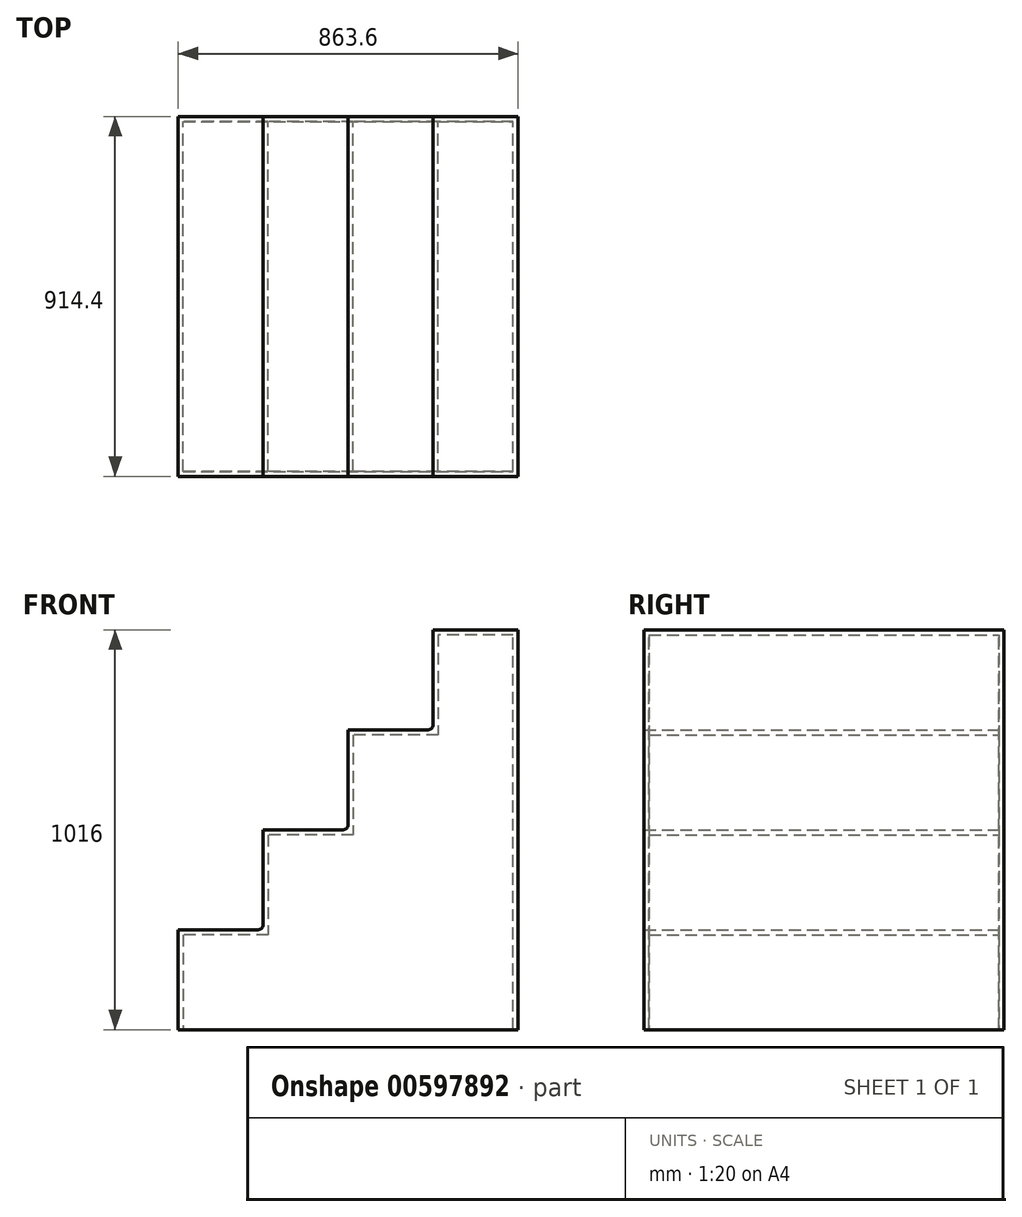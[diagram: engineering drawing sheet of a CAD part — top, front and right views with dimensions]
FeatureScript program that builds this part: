
annotation { "Feature Type Name" : "Feature", "Feature Type Description" : "" }
export const myFeature = defineFeature(function(context is Context, id is Id, definition is map)
    precondition{}
    {
        {
            var Q0;
            Q0=qCreatedBy(makeId("Front.planeOp"),FACE);
            var sketch = newSketch(context, id + "F0", { "sketchPlane" : qUnion([Q0])});
            skLineSegment(sketch, "E0", {"start": v(0, 0) * mm, "end": v(0, 1016) * mm});
            skLineSegment(sketch, "E1", {"start": v(0, 1016) * mm, "end": v(-215.9, 1016) * mm});
            skLineSegment(sketch, "E2", {"start": v(-215.9, 1016) * mm, "end": v(-215.9, 762) * mm});
            skLineSegment(sketch, "E3", {"start": v(-215.9, 762) * mm, "end": v(-431.8, 762) * mm});
            skLineSegment(sketch, "E4", {"start": v(-431.8, 762) * mm, "end": v(-431.8, 508) * mm});
            skLineSegment(sketch, "E5", {"start": v(-431.8, 508) * mm, "end": v(-647.7, 508) * mm});
            skLineSegment(sketch, "E6", {"start": v(-647.7, 508) * mm, "end": v(-647.7, 254) * mm});
            skLineSegment(sketch, "E7", {"start": v(-647.7, 254) * mm, "end": v(-863.6, 254) * mm});
            skLineSegment(sketch, "E8", {"start": v(-863.6, 254) * mm, "end": v(-863.6, 0) * mm});
            skLineSegment(sketch, "E9", {"start": v(-863.6, 0) * mm, "end": v(0, 0) * mm});
            skSolve(sketch);
        }
        {
            var Q0;
            Q0 = qSketchRegion(id + "F0", true);
            extrude(context, id + "F1", {"entities" : qUnion([Q0]), "depth" : 914.4 * mm, "offsetDistance" : 25.4 * mm});
        }
        {
            var Q0;
            Q0=makeQuery(id+"F1.opExtrude","SWEPT_FACE",FACE,{"disambiguationData":[OSD([sQuery(id+"F0.wireOp",EDGE,"E9")])]});
            shell(context, id + "F2", {"entities" : qUnion([Q0]), "thickness" : 12.7 * mm});
        }
        {
            var Q0;
            Q0=makeQuery(id+"F1.opExtrude","SWEPT_EDGE",EDGE,{"disambiguationData":[OSD([sQuery(id+"F0.wireOp",EDGE,"E6"),sQuery(id+"F0.wireOp",EDGE,"E7")])]});
            var Q1;
            Q1=makeQuery(id+"F1.opExtrude","SWEPT_EDGE",EDGE,{"disambiguationData":[OSD([sQuery(id+"F0.wireOp",EDGE,"E4"),sQuery(id+"F0.wireOp",EDGE,"E5")])]});
            var Q2;
            Q2=makeQuery(id+"F1.opExtrude","SWEPT_EDGE",EDGE,{"disambiguationData":[OSD([sQuery(id+"F0.wireOp",EDGE,"E2"),sQuery(id+"F0.wireOp",EDGE,"E3")])]});
            fillet(context, id + "F3", {"entities" : qUnion([Q0, Q1, Q2]), "radius" : 12.7 * mm, "tangentPropagation" : true, "allowEdgeOverflow" : false});
        }
    });
